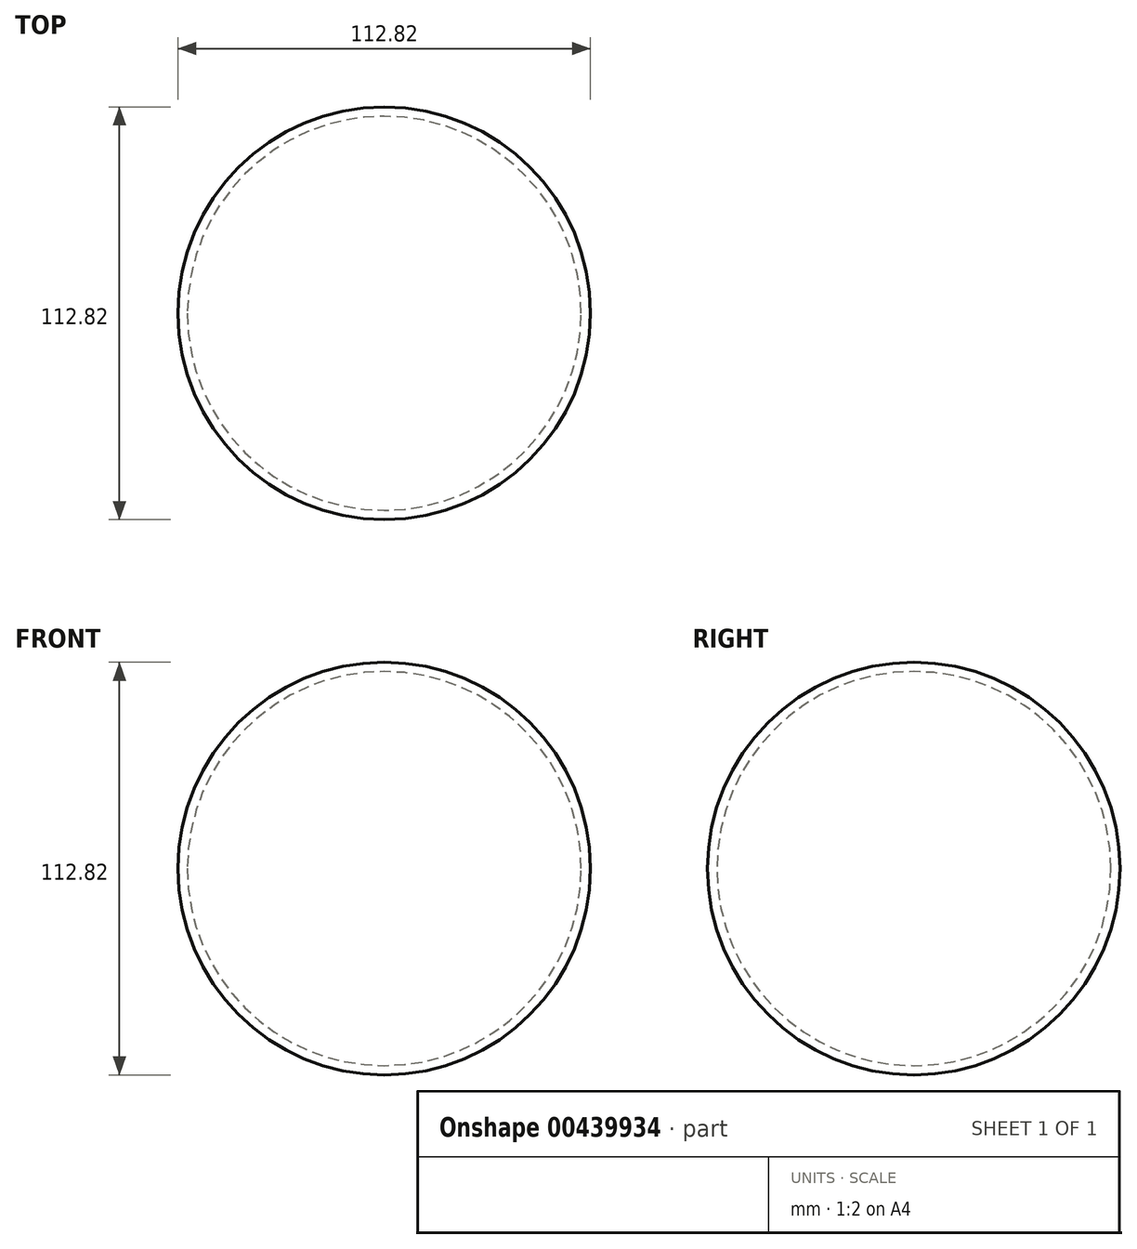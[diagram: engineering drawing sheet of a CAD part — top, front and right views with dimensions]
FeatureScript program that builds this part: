
annotation { "Feature Type Name" : "Feature", "Feature Type Description" : "" }
export const myFeature = defineFeature(function(context is Context, id is Id, definition is map)
    precondition{}
    {
        {
            var Q0;
            Q0=qCreatedBy(makeId("Front.planeOp"),FACE);
            var sketch = newSketch(context, id + "F0", { "sketchPlane" : qUnion([Q0])});
            skLineSegment(sketch, "E0", {"start": v(-121, 0) * mm, "end": v(100.6, 0) * mm});
            skCircle(sketch, "E1", {"center": v(0, 0) * mm, "radius": 56.4 * mm});
            skSolve(sketch);
        }
        {
            var Q0;
            {var subQ0=sQuery(id+"F0.wireOp",EDGE,"E1");var subQ1=sQuery(id+"F0.wireOp",EDGE,"E0");var subQ2=makeQuery(id+"F0.imprint","INTERSECT",VERTEX,{"disambiguationData":[OD(0.0)],"derivedFrom":[subQ1,subQ0]});Q0=makeQuery(id+"F0.imprint","IMPRINT",FACE,{"disambiguationData":[TD([[makeQuery(id+"F0.imprint","IMPRINT",EDGE,{"disambiguationData":[TD([[subQ2,-1.0]])],"derivedFrom":subQ1}),1.0]])]});}
            var Q1;
            Q1=sQuery(id+"F0.wireOp",EDGE,"E0");
            revolve(context, id + "F1", {"entities" : qUnion([Q0]), "axis" : qUnion([Q1]), "revolveType" : RevolveType.FULL});
        }
        {
            var Q0;
            Q0=makeQuery(id+"F1.opRevolve","SWEPT_FACE",FACE,{"disambiguationData":[OSD([sQuery(id+"F0.wireOp",EDGE,"E1")])]});
            var Q1;
            Q1=makeQuery(id+"F1.opRevolve","SWEPT_BODY",BODY,{"disambiguationData":[OSD([sQuery(id+"F0.wireOp",EDGE,"E0"),sQuery(id+"F0.wireOp",EDGE,"E1")])]});
            shell(context, id + "F2", {"isHollow" : true, "entities" : qUnion([Q0]), "parts" : qUnion([Q1]), "thickness" : 2.54 * mm});
        }
    });
